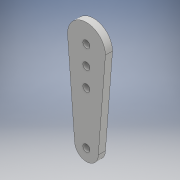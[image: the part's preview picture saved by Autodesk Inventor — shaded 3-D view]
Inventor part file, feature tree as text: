
AUTODESK INVENTOR PART (.ipt)
format: ipt  version: 2018 (Build 220112000, 112)  size: 112,128 bytes
history: native  units: mm
features: other x1, extrude x1, sketch x1
ambient origin geometry x8: Origin, YZ Plane, XZ Plane, XY Plane, X Axis, Y Axis, Z Axis, Center Point
bodies: Body1 (feature_tree)
feature tree (3):
  other  "Sólido1"
  extrude  "Extrusión1"  Depth=3.0mm
  sketch  "Boceto1"  dims[d26=30.0mm d125=16.0mm d126=3.0mm d172=3.0mm d173=0.0mm]
